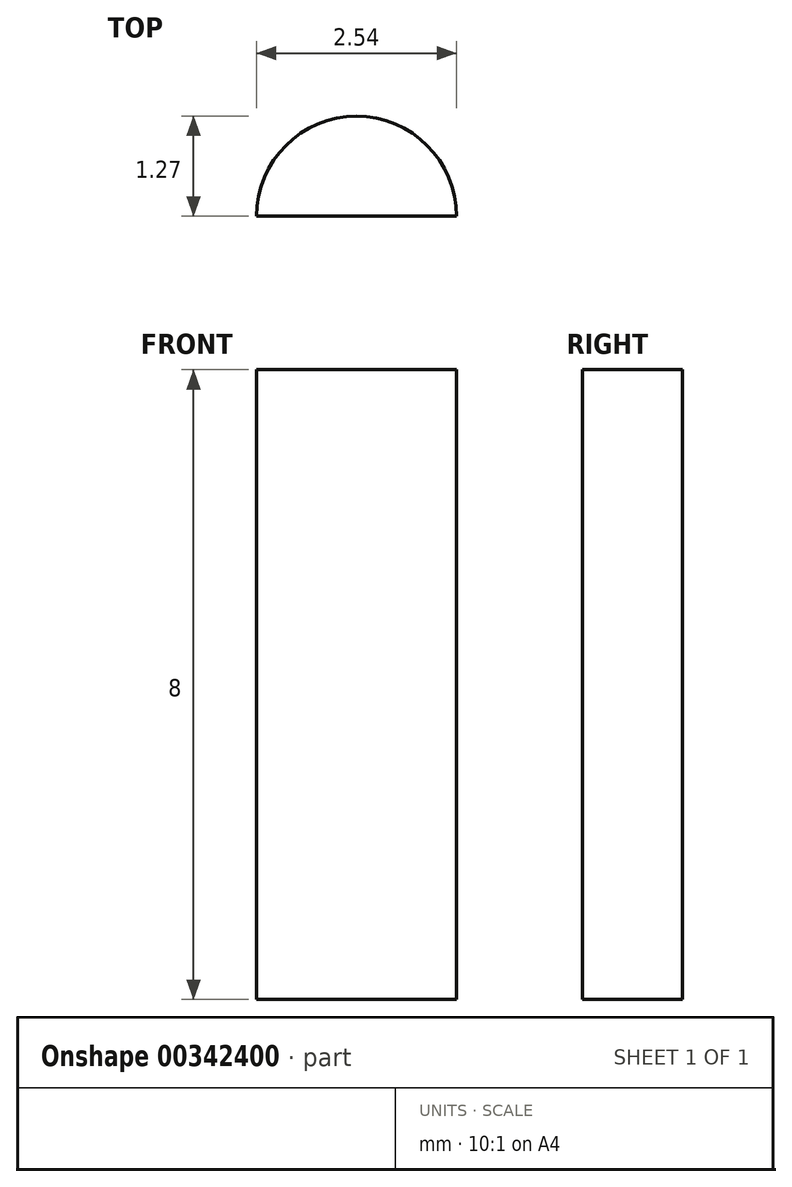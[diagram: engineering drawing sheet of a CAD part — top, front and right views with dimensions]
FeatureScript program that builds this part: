
annotation { "Feature Type Name" : "Feature", "Feature Type Description" : "" }
export const myFeature = defineFeature(function(context is Context, id is Id, definition is map)
    precondition{}
    {
        {
            var Q0;
            Q0=qCreatedBy(makeId("Top.planeOp"),FACE);
            var sketch = newSketch(context, id + "F0", { "sketchPlane" : qUnion([Q0])});
            skCircle(sketch, "E0", {"center": v(0, 0) * mm, "radius": 1.27 * mm});
            skSolve(sketch);
        }
        {
            var Q0;
            Q0 = qSketchRegion(id + "F0", true);
            extrude(context, id + "F1", {"entities" : qUnion([Q0]), "depth" : 8 * mm});
        }
        {
            var Q0;
            Q0=makeQuery(id+"F1.opExtrude","CAP_FACE",FACE,{"disambiguationData":[OSD([sQuery(id+"F0.wireOp",EDGE,"E0")])],"isStart":false});
            cPlane(context, id + "F2", {"entities" : qUnion([Q0]), "cplaneType" : CPlaneType.OFFSET, "offset" : 25.4 * mm, "width" : 152.4 * mm, "height" : 152.4 * mm});
        }
        {
            var Q0;
            Q0=qCreatedBy(id+"F2.planeOp",FACE);
            var sketch = newSketch(context, id + "F3", { "sketchPlane" : qUnion([Q0])});
            skArc(sketch, "E1", {"start": v(-1.35, 0) * mm, "mid": v(0, -1.5) * mm, "end": v(1.35, 0) * mm});
            skLineSegment(sketch, "E2", {"start": v(-1.35, 0) * mm, "end": v(1.35, 0) * mm});
            skSolve(sketch);
        }
        {
            var Q0;
            Q0 = qSketchRegion(id + "F3", true);
            extrude(context, id + "F4", {"entities" : qUnion([Q0]), "operationType" : NewBodyOperationType.REMOVE, "oppositeDirection" : true, "depth" : 52.86 * mm});
        }
    });
